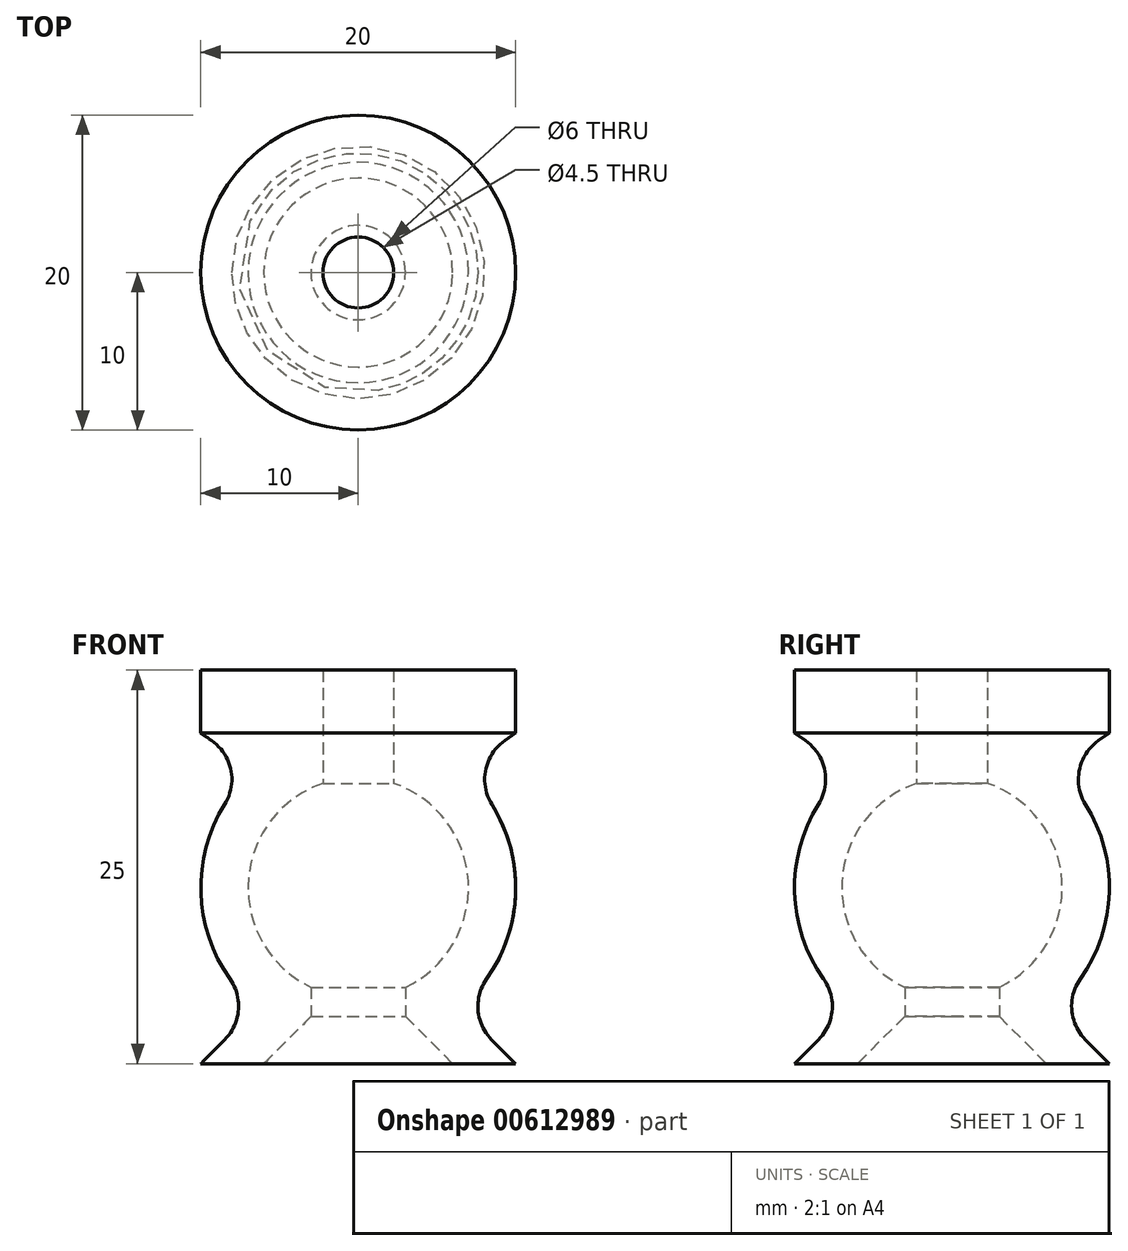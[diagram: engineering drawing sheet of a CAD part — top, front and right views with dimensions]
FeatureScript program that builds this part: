
annotation { "Feature Type Name" : "Feature", "Feature Type Description" : "" }
export const myFeature = defineFeature(function(context is Context, id is Id, definition is map)
    precondition{}
    {
        {
            var Q0;
            Q0=qCreatedBy(makeId("Front.planeOp"),FACE);
            var sketch = newSketch(context, id + "F0", { "sketchPlane" : qUnion([Q0])});
            skLineSegment(sketch, "E0", {"start": v(0, 0) * mm, "end": v(0, 50) * mm, "construction": true});
            skLineSegment(sketch, "E1", {"start": v(6, 0) * mm, "end": v(10, 0) * mm});
            skLineSegment(sketch, "E2", {"start": v(10, 0) * mm, "end": v(6.46, 3.54) * mm});
            skLineSegment(sketch, "E3", {"start": v(6, 0) * mm, "end": v(1.63, 4.37) * mm});
            skLineSegment(sketch, "E4", {"start": v(2.25, 25) * mm, "end": v(10, 25) * mm});
            skPoint(sketch, "E4.startSnap0", {"position": v(0, 25) * mm});
            skLineSegment(sketch, "E5", {"start": v(2.25, 25) * mm, "end": v(2.25, 17.8) * mm});
            skLineSegment(sketch, "E6", {"start": v(10, 25) * mm, "end": v(10, 21) * mm});
            skLineSegment(sketch, "E7", {"start": v(10, 21) * mm, "end": v(6.64, 18.65) * mm});
            skArc(sketch, "E8", {"start": v(2.25, 17.8) * mm, "mid": v(-7, 11.5) * mm, "end": v(1.63, 4.37) * mm, "construction": true});
            skArc(sketch, "E9", {"start": v(1.63, 4.37) * mm, "mid": v(7, 10.85) * mm, "end": v(2.25, 17.8) * mm});
            skArc(sketch, "E10", {"start": v(6.64, 18.65) * mm, "mid": v(-10, 11.3) * mm, "end": v(6.46, 3.54) * mm, "construction": true});
            skArc(sketch, "E11", {"start": v(6.46, 3.54) * mm, "mid": v(10, 11.05) * mm, "end": v(6.64, 18.65) * mm});
            skLineSegment(sketch, "E12", {"start": v(3, 3) * mm, "end": v(3, 4.85) * mm});
            skSolve(sketch);
        }
        {
            var Q0;
            {var subQ1=sQuery(id+"F0.wireOp",EDGE,"E1");Q0=makeQuery(id+"F0.imprint","IMPRINT",FACE,{"disambiguationData":[TD([[makeQuery(id+"F0.imprint","IMPRINT",EDGE,{"derivedFrom":subQ1}),1.0]])]});}
            var Q1;
            Q1=sQuery(id+"F0.wireOp",EDGE,"E0");
            revolve(context, id + "F1", {"entities" : qUnion([Q0]), "axis" : qUnion([Q1]), "revolveType" : RevolveType.FULL});
        }
        {
            var Q0;
            Q0=makeQuery(id+"F1.opRevolve","SWEPT_EDGE",EDGE,{"disambiguationData":[OSD([sQuery(id+"F0.wireOp",EDGE,"E7"),sQuery(id+"F0.wireOp",EDGE,"E11")])]});
            var Q1;
            Q1=makeQuery(id+"F1.opRevolve","SWEPT_EDGE",EDGE,{"disambiguationData":[OSD([sQuery(id+"F0.wireOp",EDGE,"E2"),sQuery(id+"F0.wireOp",EDGE,"E11")])]});
            fillet(context, id + "F2", {"entities" : qUnion([Q0, Q1]), "radius" : 3 * mm, "tangentPropagation" : true, "allowEdgeOverflow" : false});
        }
    });
